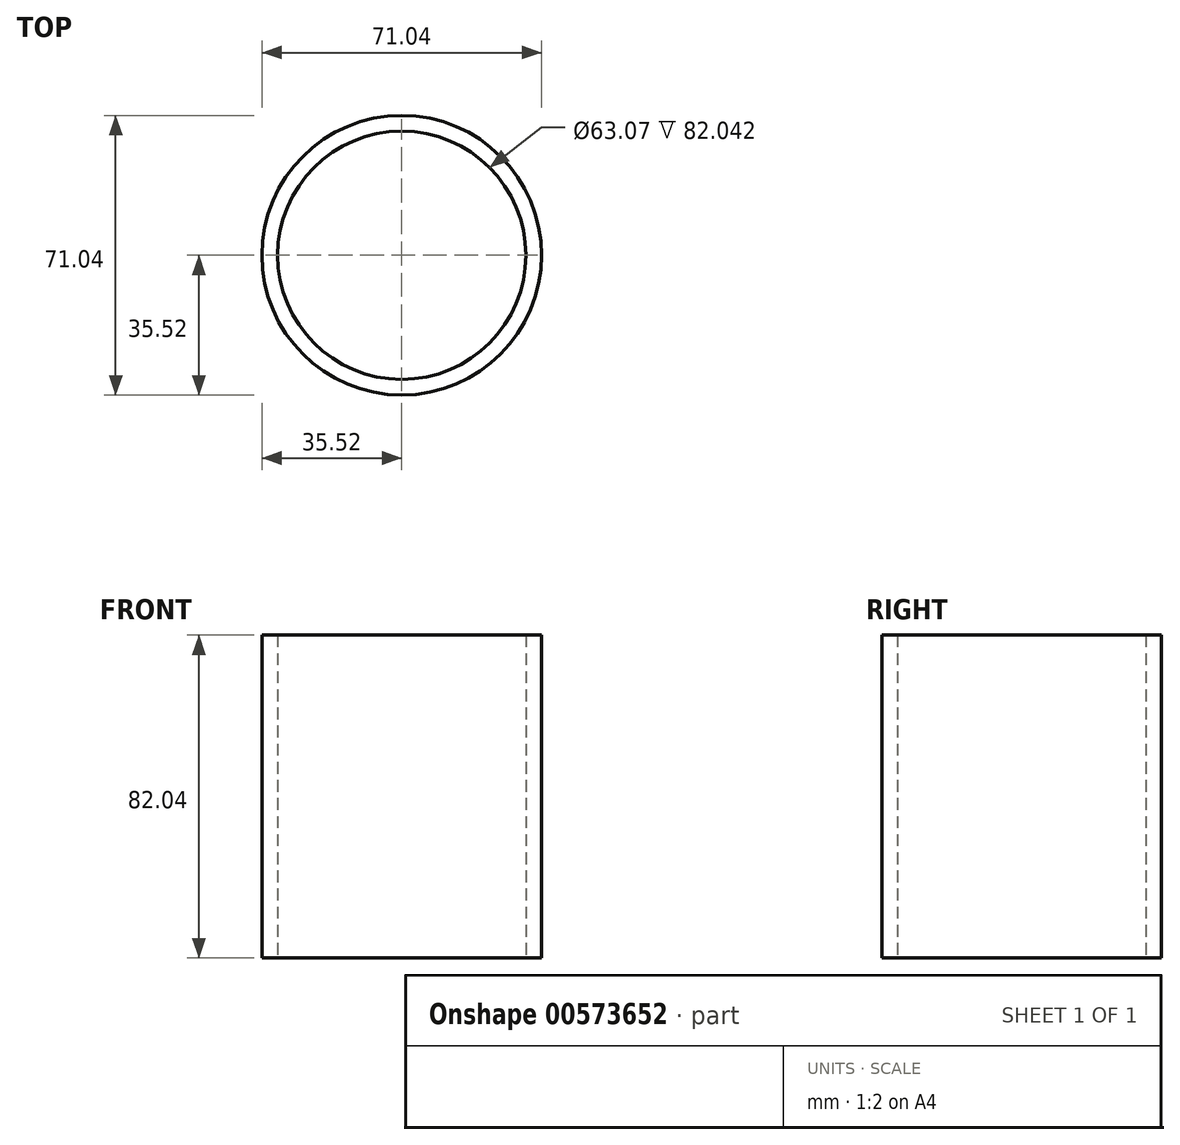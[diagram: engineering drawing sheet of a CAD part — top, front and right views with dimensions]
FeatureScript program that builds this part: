
annotation { "Feature Type Name" : "Feature", "Feature Type Description" : "" }
export const myFeature = defineFeature(function(context is Context, id is Id, definition is map)
    precondition{}
    {
        {
            var Q0;
            Q0=qCreatedBy(makeId("Top.planeOp"),FACE);
            var sketch = newSketch(context, id + "F0", { "sketchPlane" : qUnion([Q0])});
            skCircle(sketch, "E0", {"center": v(0, 0) * mm, "radius": 35.52 * mm});
            skCircle(sketch, "E1", {"center": v(0, 0) * mm, "radius": 31.53 * mm});
            skCircle(sketch, "E2", {"center": v(0, 0) * mm, "radius": 30.93 * mm});
            skSolve(sketch);
        }
        {
            var Q0;
            Q0 = qSketchRegion(id + "F0", true);
            extrude(context, id + "F1", {"entities" : qUnion([Q0]), "depth" : 82.04 * mm, "offsetDistance" : 25.4 * mm});
        }
    });
